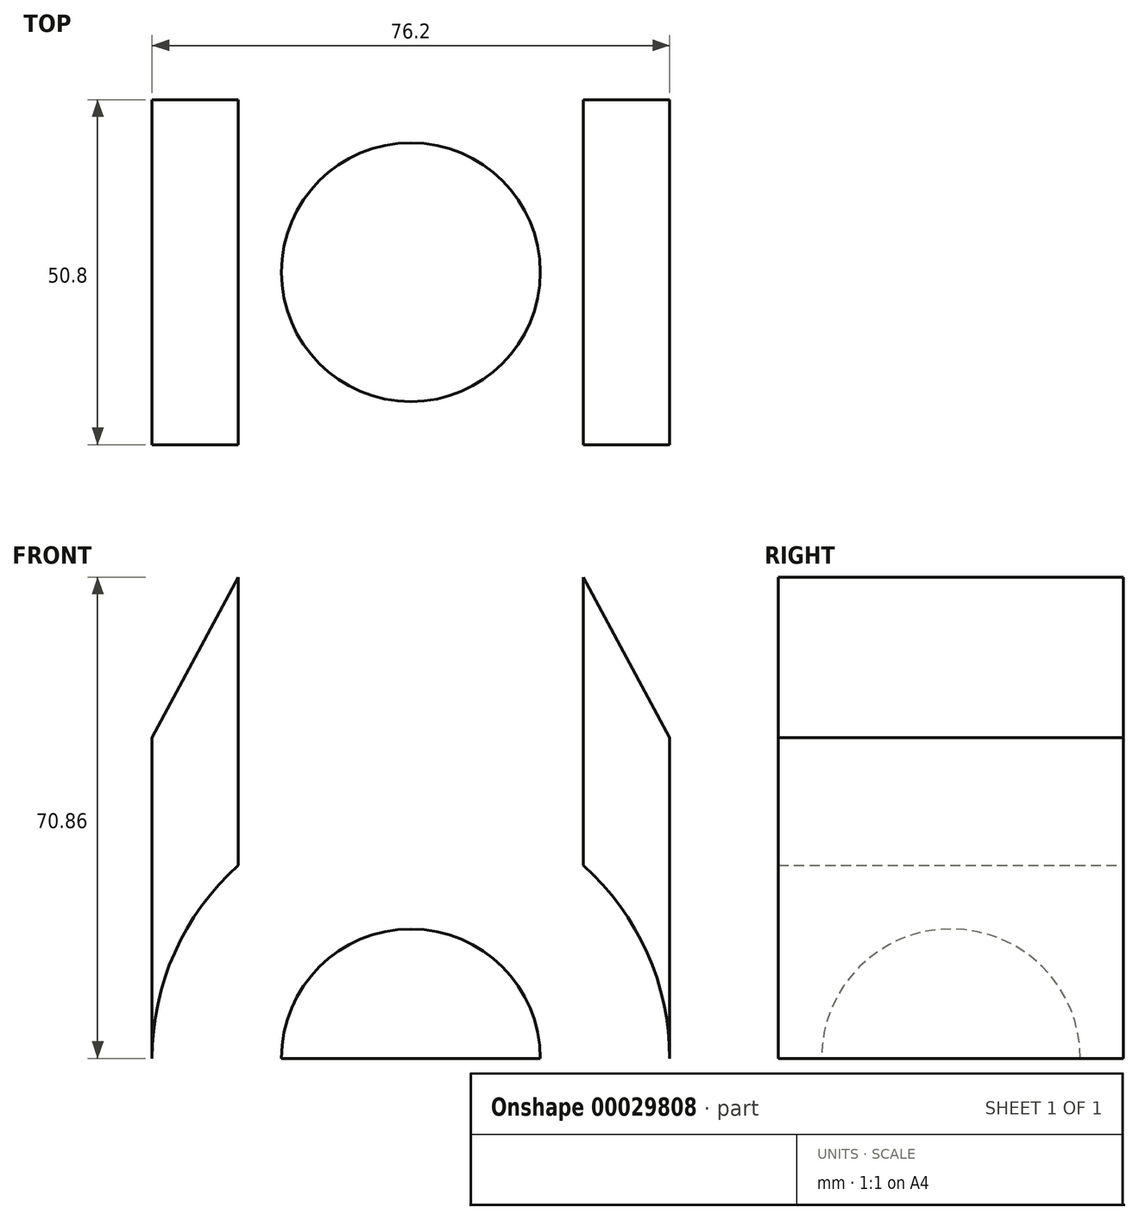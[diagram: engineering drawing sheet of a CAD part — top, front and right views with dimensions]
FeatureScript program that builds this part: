
annotation { "Feature Type Name" : "Feature", "Feature Type Description" : "" }
export const myFeature = defineFeature(function(context is Context, id is Id, definition is map)
    precondition{}
    {
        {
            var Q0;
            Q0=qCreatedBy(makeId("Front.planeOp"),FACE);
            var sketch = newSketch(context, id + "F0", { "sketchPlane" : qUnion([Q0])});
            skLineSegment(sketch, "E0.rect.bottom", {"start": v(25.4, -7.23) * mm, "end": v(-25.4, -7.23) * mm});
            skLineSegment(sketch, "E0.rect.left", {"start": v(25.4, -7.23) * mm, "end": v(25.4, 7.23) * mm});
            skLineSegment(sketch, "E0.rect.right", {"start": v(-25.4, -7.23) * mm, "end": v(-25.4, 7.23) * mm});
            skPoint(sketch, "E0.rect.middle", {"position": v(0, 0) * mm});
            skLineSegment(sketch, "E1.bottom", {"start": v(-25.4, -7.23) * mm, "end": v(-38.1, -7.23) * mm});
            skLineSegment(sketch, "E1.top", {"start": v(-25.4, 40) * mm, "end": v(-38.1, 40) * mm});
            skLineSegment(sketch, "E1.left", {"start": v(-25.4, -7.23) * mm, "end": v(-25.4, 40) * mm});
            skLineSegment(sketch, "E1.right", {"start": v(-38.1, -7.23) * mm, "end": v(-38.1, 40) * mm});
            skLineSegment(sketch, "E2.bottom", {"start": v(25.4, -7.23) * mm, "end": v(38.1, -7.23) * mm});
            skLineSegment(sketch, "E2.top", {"start": v(25.4, 40) * mm, "end": v(38.1, 40) * mm});
            skLineSegment(sketch, "E2.left", {"start": v(25.4, -7.23) * mm, "end": v(25.4, 40) * mm});
            skLineSegment(sketch, "E2.right", {"start": v(38.1, -7.23) * mm, "end": v(38.1, 40) * mm});
            skLineSegment(sketch, "E3", {"start": v(-38.1, 40) * mm, "end": v(-25.4, 63.63) * mm});
            skLineSegment(sketch, "E4", {"start": v(-25.4, 63.63) * mm, "end": v(-25.4, 40) * mm});
            skLineSegment(sketch, "E5", {"start": v(25.4, 40) * mm, "end": v(25.4, 63.63) * mm});
            skLineSegment(sketch, "E6", {"start": v(25.4, 63.63) * mm, "end": v(38.1, 40) * mm});
            skLineSegment(sketch, "E7", {"start": v(-25.4, 12.04) * mm, "end": v(25.4, 12.04) * mm});
            skSolve(sketch);
        }
        {
            var Q0;
            {var subQ2=sQuery(id+"F0.wireOp",EDGE,"E0.rect.bottom");Q0=makeQuery(id+"F0.imprint","IMPRINT",FACE,{"disambiguationData":[TD([[makeQuery(id+"F0.imprint","IMPRINT",EDGE,{"derivedFrom":subQ2}),-1.0]])]});}
            var Q1;
            {var subQ3=sQuery(id+"F0.wireOp",EDGE,"E1.bottom");Q1=makeQuery(id+"F0.imprint","IMPRINT",FACE,{"disambiguationData":[TD([[makeQuery(id+"F0.imprint","IMPRINT",EDGE,{"derivedFrom":subQ3}),-1.0]])]});}
            var Q2;
            {var subQ3=sQuery(id+"F0.wireOp",EDGE,"E2.bottom");Q2=makeQuery(id+"F0.imprint","IMPRINT",FACE,{"disambiguationData":[TD([[makeQuery(id+"F0.imprint","IMPRINT",EDGE,{"derivedFrom":subQ3}),1.0]])]});}
            var Q3;
            Q3=makeQuery(id+"F0.imprint","IMPRINT",FACE,{"disambiguationData":[TD([[makeQuery(id+"F0.imprint","IMPRINT",EDGE,{"derivedFrom":sQuery(id+"F0.wireOp",EDGE,"E2.top")}),1.0]])]});
            var Q4;
            Q4=makeQuery(id+"F0.imprint","IMPRINT",FACE,{"disambiguationData":[TD([[makeQuery(id+"F0.imprint","IMPRINT",EDGE,{"derivedFrom":sQuery(id+"F0.wireOp",EDGE,"E1.top")}),-1.0]])]});
            extrude(context, id + "F1", {"entities" : qUnion([Q0, Q1, Q2, Q3, Q4]), "depth" : 50.8 * mm});
        }
        {
            var Q0;
            Q0=makeQuery(id+"F1.opExtrude","SWEPT_FACE",FACE,{"disambiguationData":[OSD([sQuery(id+"F0.wireOp",EDGE,"E0.rect.bottom"),sQuery(id+"F0.wireOp",EDGE,"E1.bottom"),sQuery(id+"F0.wireOp",EDGE,"E2.bottom")])]});
            var sketch = newSketch(context, id + "F2", { "sketchPlane" : qUnion([Q0])});
            skLineSegment(sketch, "E8", {"start": v(-38.1, 25.4) * mm, "end": v(38.1, 25.4) * mm});
            skLineSegment(sketch, "E9", {"start": v(0, 50.8) * mm, "end": v(0, 0) * mm});
            skCircle(sketch, "E10", {"center": v(0, 25.4) * mm, "radius": 19.05 * mm});
            skSolve(sketch);
        }
        {
            var Q0;
            {var subQ0=sQuery(id+"F2.wireOp",EDGE,"E10");var subQ3=sQuery(id+"F2.wireOp",EDGE,"E8");var subQ4=makeQuery(id+"F2.imprint","INTERSECT",VERTEX,{"disambiguationData":[OD(0.0)],"derivedFrom":[subQ3,subQ0]});Q0=makeQuery(id+"F2.imprint","IMPRINT",FACE,{"disambiguationData":[TD([[makeQuery(id+"F2.imprint","IMPRINT",EDGE,{"disambiguationData":[TD([[subQ4,-1.0]])],"derivedFrom":subQ3}),1.0]])]});}
            var Q1;
            {var subQ0=sQuery(id+"F2.wireOp",EDGE,"E10");var subQ3=sQuery(id+"F2.wireOp",EDGE,"E8");var subQ4=makeQuery(id+"F2.imprint","INTERSECT",VERTEX,{"disambiguationData":[OD(0.0)],"derivedFrom":[subQ3,subQ0]});Q1=makeQuery(id+"F2.imprint","IMPRINT",FACE,{"disambiguationData":[TD([[makeQuery(id+"F2.imprint","IMPRINT",EDGE,{"disambiguationData":[TD([[subQ4,-1.0]])],"derivedFrom":subQ3}),-1.0]])]});}
            var Q2;
            Q2=sQuery(id+"F2.wireOp",EDGE,"E9");
            revolve(context, id + "F3", {"operationType" : NewBodyOperationType.REMOVE, "entities" : qUnion([Q0, Q1]), "axis" : qUnion([Q2]), "revolveType" : RevolveType.FULL, "oppositeDirection" : true});
        }
    });
